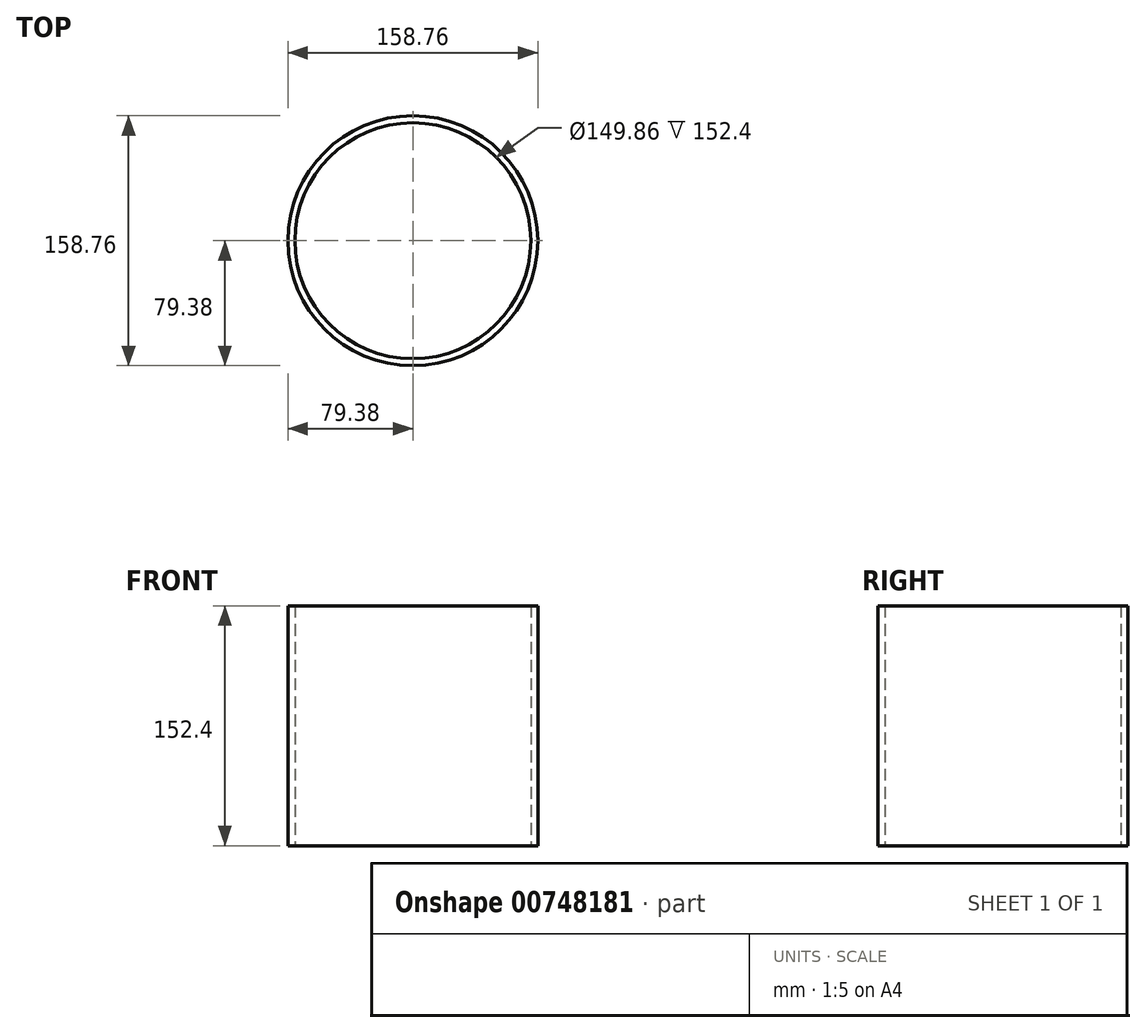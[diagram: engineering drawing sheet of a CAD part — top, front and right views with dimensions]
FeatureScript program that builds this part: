
annotation { "Feature Type Name" : "Feature", "Feature Type Description" : "" }
export const myFeature = defineFeature(function(context is Context, id is Id, definition is map)
    precondition{}
    {
        {
            var Q0;
            Q0=qCreatedBy(makeId("Top.planeOp"),FACE);
            var sketch = newSketch(context, id + "F0", { "sketchPlane" : qUnion([Q0])});
            skCircle(sketch, "E0", {"center": v(0, 0) * mm, "radius": 74.93 * mm});
            skCircle(sketch, "E1", {"center": v(0, 0) * mm, "radius": 79.38 * mm});
            skSolve(sketch);
        }
        {
            var Q0;
            Q0=makeQuery(id+"F0.imprint","IMPRINT",FACE,{"disambiguationData":[TD([[makeQuery(id+"F0.imprint","IMPRINT",EDGE,{"derivedFrom":sQuery(id+"F0.wireOp",EDGE,"E0")}),-1.0]])]});
            extrude(context, id + "F1", {"entities" : qUnion([Q0]), "depth" : 152.4 * mm, "offsetDistance" : 25.4 * mm});
        }
    });
